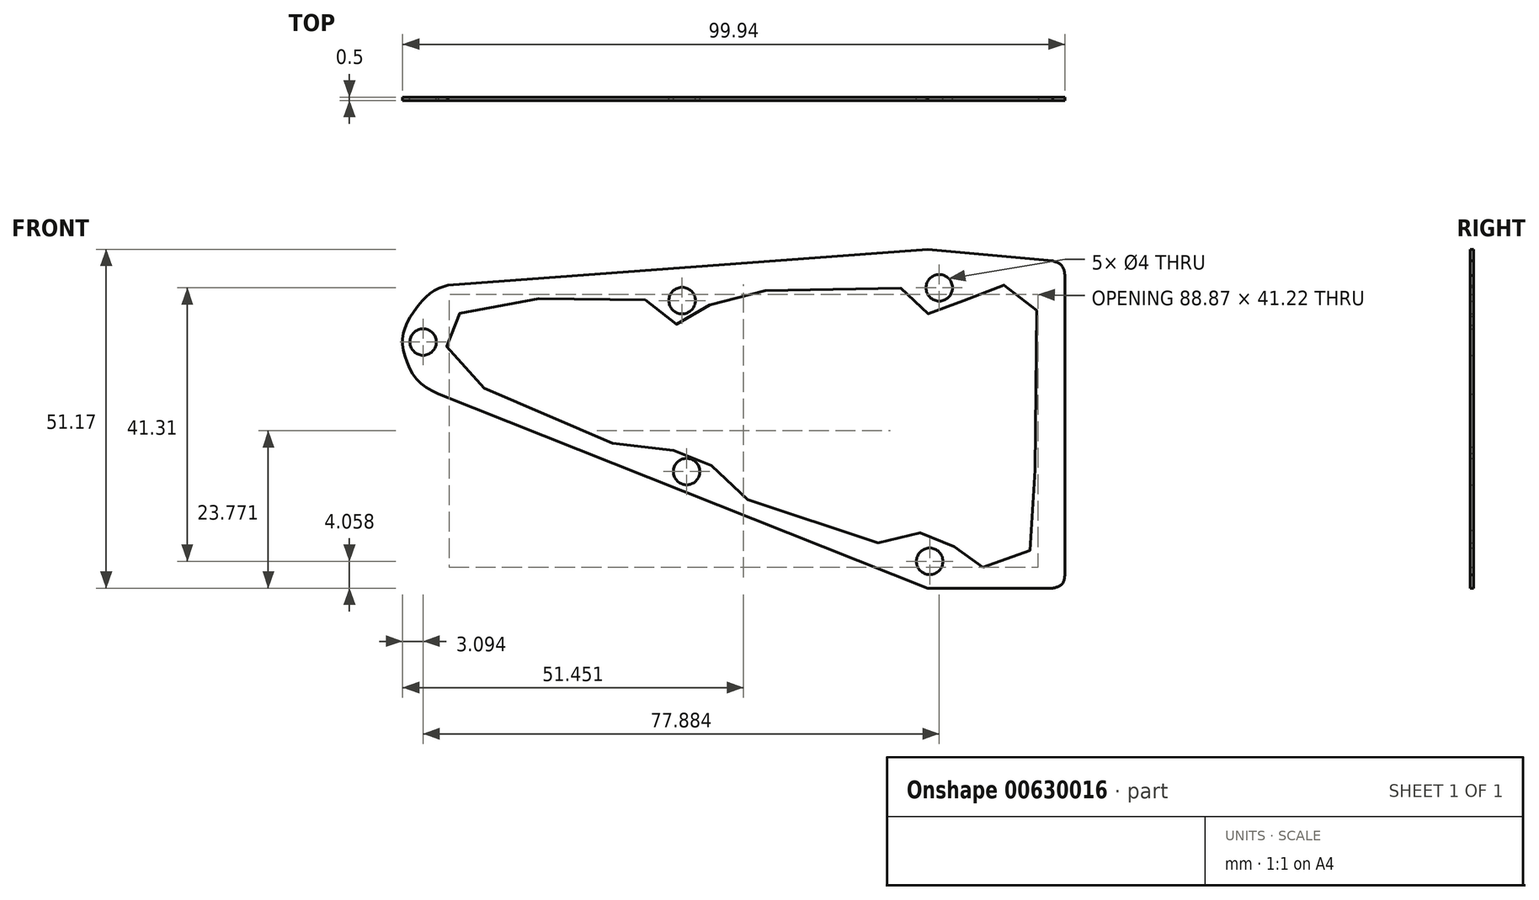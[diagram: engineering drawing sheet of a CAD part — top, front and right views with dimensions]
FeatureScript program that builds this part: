
annotation { "Feature Type Name" : "Feature", "Feature Type Description" : "" }
export const myFeature = defineFeature(function(context is Context, id is Id, definition is map)
    precondition{}
    {
        {
            var Q0;
            Q0=qCreatedBy(makeId("Front.planeOp"),FACE);
            var sketch = newSketch(context, id + "F0", { "sketchPlane" : qUnion([Q0])});
            skPoint(sketch, "E0.middle", {"position": v(0, 0) * mm});
            skCircle(sketch, "E1", {"center": v(-50.7, 15) * mm, "radius": 2 * mm});
            skCircle(sketch, "E2", {"center": v(-10.93, -4.58) * mm, "radius": 2 * mm});
            skCircle(sketch, "E3", {"center": v(25.74, -18.12) * mm, "radius": 2 * mm});
            skCircle(sketch, "E4", {"center": v(-11.6, 21.25) * mm, "radius": 2 * mm});
            skCircle(sketch, "E5", {"center": v(27.19, 23.19) * mm, "radius": 2 * mm});
            skLineSegment(sketch, "E6", {"start": v(-46.92, 23.58) * mm, "end": v(25.45, 29) * mm});
            skLineSegment(sketch, "E7", {"start": v(25.45, 29) * mm, "end": v(44.31, 27.25) * mm});
            skLineSegment(sketch, "E8", {"start": v(-48.37, 7.13) * mm, "end": v(25.45, -22.18) * mm});
            skLineSegment(sketch, "E9", {"start": v(25.45, -22.18) * mm, "end": v(44.31, -22.18) * mm});
            skLineSegment(sketch, "E10", {"start": v(46.15, 25.03) * mm, "end": v(46.15, -20.15) * mm});
            skFitSpline(sketch, "E11", {"points": [v(46.15, -20.15) * mm, v(45.71, -21.57) * mm, v(44.31, -22.18) * mm], "startDerivative": vector(-0.41, -3.26) * mm, "endDerivative": vector(-3.26, -0.81) * mm});
            skFitSpline(sketch, "E12", {"points": [v(44.31, 27.25) * mm, v(45.68, 26.51) * mm, v(46.15, 25.03) * mm], "startDerivative": vector(3.2, -1.1) * mm, "endDerivative": vector(0.48, -3.35) * mm});
            skFitSpline(sketch, "E13", {"points": [v(-46.92, 23.58) * mm, v(-49.53, 22.4) * mm, v(-50.79, 21.25) * mm, v(-52.55, 18.93) * mm, v(-53.48, 16.97) * mm, v(-53.79, 15.06) * mm, v(-53.44, 12.92) * mm, v(-52.47, 10.53) * mm, v(-50.89, 8.64) * mm, v(-48.37, 7.13) * mm], "startDerivative": vector(-38.63, -10.82) * mm, "endDerivative": vector(22.49, -11.17) * mm});
            skFitSpline(sketch, "E14", {"points": [v(33.77, -19.02) * mm, v(37.99, -18.98) * mm, v(40.22, -18.04) * mm, v(41.32, -13.9) * mm, v(41.46, -8.98) * mm, v(42, 18.79) * mm, v(40.39, 23.02) * mm, v(38.59, 23.58) * mm, v(36.98, 23.59) * mm, v(34.88, 23.47) * mm, v(32.33, 22.65) * mm, v(30.82, 21.15) * mm, v(29.73, 19.83) * mm, v(27.8, 18.96) * mm, v(25.88, 19.09) * mm, v(24.16, 20.12) * mm, v(23.08, 21.28) * mm, v(22.1, 22.58) * mm, v(20.39, 23.34) * mm, v(-2.17, 22.54) * mm, v(-4.7, 22.19) * mm, v(-7.02, 21.14) * mm, v(-8.07, 19.53) * mm, v(-9.12, 18.27) * mm, v(-11.09, 17.56) * mm, v(-13.7, 18.09) * mm, v(-15.07, 19.24) * mm, v(-15.93, 20.25) * mm, v(-17.35, 21.52) * mm, v(-19.9, 22.18) * mm, v(-42.22, 20.56) * mm, v(-43.89, 19.98) * mm, v(-45.44, 19.12) * mm, v(-46.54, 17.8) * mm, v(-47, 16.47) * mm, v(-47.12, 15.06) * mm, v(-47.05, 13.48) * mm, v(-46.8, 12.62) * mm, v(-45.23, 10.38) * mm, v(-25.36, 0.95) * mm, v(-18.04, -1.48) * mm, v(-14.04, -1.7) * mm, v(-11.32, -0.92) * mm, v(-8.73, -1.38) * mm, v(-7.39, -3.12) * mm, v(-6.9, -5.1) * mm, v(-6.54, -6.23) * mm, v(-5.18, -7.27) * mm, v(15.88, -15) * mm, v(19.7, -15.28) * mm, v(21.54, -15.06) * mm, v(23.78, -14.08) * mm, v(25.6, -13.46) * mm, v(27.47, -13.95) * mm, v(28.84, -14.96) * mm, v(29.78, -16.7) * mm, v(30.6, -18.2) * mm, v(31.87, -18.88) * mm, v(33.77, -19.02) * mm]});
            skSolve(sketch);
        }
        {
            var Q0;
            Q0 = qSketchRegion(id + "F0", true);
            extrude(context, id + "F1", {"entities" : qUnion([Q0]), "depth" : 0.5 * mm, "offsetDistance" : 25 * mm});
        }
    });
